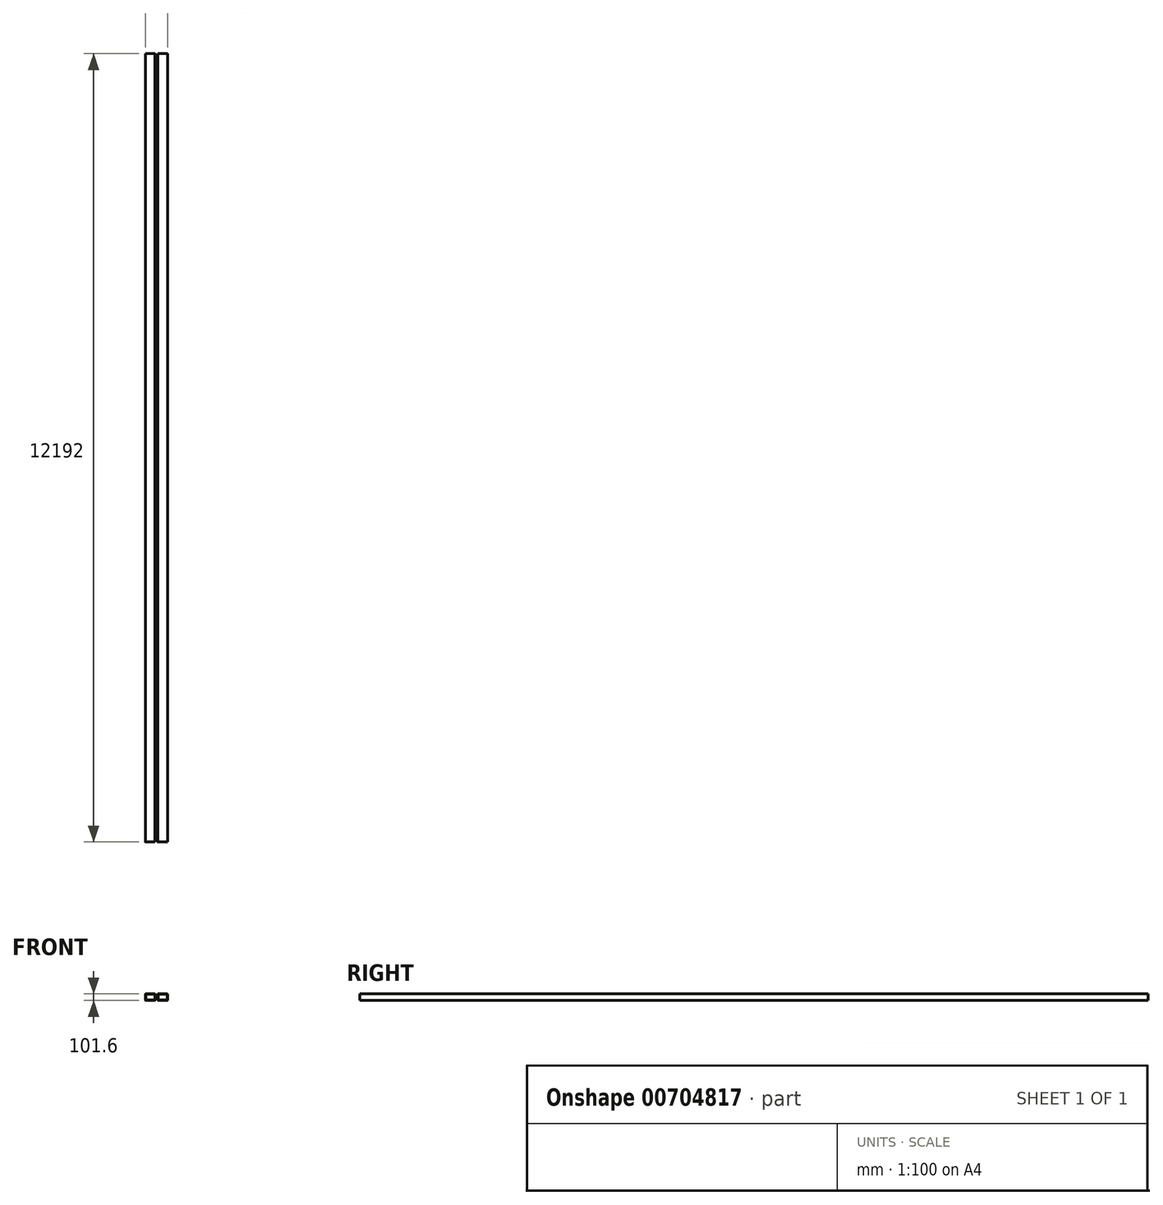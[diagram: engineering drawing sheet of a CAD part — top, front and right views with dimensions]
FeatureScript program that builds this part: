
annotation { "Feature Type Name" : "Feature", "Feature Type Description" : "" }
export const myFeature = defineFeature(function(context is Context, id is Id, definition is map)
    precondition{}
    {
        {
            var Q0;
            Q0=qCreatedBy(makeId("Front.planeOp"),FACE);
            var sketch = newSketch(context, id + "F0", { "sketchPlane" : qUnion([Q0])});
            skLineSegment(sketch, "E0.bottom", {"start": v(-6.35, 0) * mm, "end": v(-146.05, 0) * mm});
            skLineSegment(sketch, "E0.top", {"start": v(-6.35, 101.6) * mm, "end": v(-146.05, 101.6) * mm});
            skLineSegment(sketch, "E0.left", {"start": v(0, 6.35) * mm, "end": v(0, 95.25) * mm});
            skLineSegment(sketch, "E0.right", {"start": v(-152.4, 6.35) * mm, "end": v(-152.4, 95.25) * mm});
            skLineSegment(sketch, "E1.bottom", {"start": v(46.37, 0) * mm, "end": v(186.07, 0) * mm});
            skLineSegment(sketch, "E1.top", {"start": v(46.37, 101.6) * mm, "end": v(186.07, 101.6) * mm});
            skLineSegment(sketch, "E1.left", {"start": v(40.02, 6.35) * mm, "end": v(40.02, 95.25) * mm});
            skLineSegment(sketch, "E1.right", {"start": v(192.42, 6.35) * mm, "end": v(192.42, 95.25) * mm});
            skLineSegment(sketch, "E2.0", {"start": v(46.37, 6.35) * mm, "end": v(46.37, 95.25) * mm});
            skLineSegment(sketch, "E2.1", {"start": v(46.37, 6.35) * mm, "end": v(186.07, 6.35) * mm});
            skLineSegment(sketch, "E2.2", {"start": v(186.07, 6.35) * mm, "end": v(186.07, 95.25) * mm});
            skLineSegment(sketch, "E2.3", {"start": v(46.37, 95.25) * mm, "end": v(186.07, 95.25) * mm});
            skLineSegment(sketch, "E3", {"start": v(-146.05, 95.25) * mm, "end": v(-6.35, 95.25) * mm});
            skLineSegment(sketch, "E4", {"start": v(-6.35, 95.25) * mm, "end": v(-6.35, 6.35) * mm});
            skLineSegment(sketch, "E5", {"start": v(-6.35, 6.35) * mm, "end": v(-146.05, 6.35) * mm});
            skLineSegment(sketch, "E6", {"start": v(-146.05, 95.25) * mm, "end": v(-146.05, 6.35) * mm});
            skPoint(sketch, "E7.visualSharp", {"position": v(-152.4, 101.6) * mm});
            skArc(sketch, "E7.filletArc", {"start": v(-146.05, 101.6) * mm, "mid": v(-150.54, 99.74) * mm, "end": v(-152.4, 95.25) * mm});
            skPoint(sketch, "E8.visualSharp", {"position": v(-152.4, 0) * mm});
            skArc(sketch, "E8.filletArc", {"start": v(-152.4, 6.35) * mm, "mid": v(-150.54, 1.86) * mm, "end": v(-146.05, 0) * mm});
            skPoint(sketch, "E9.visualSharp", {"position": v(0, 0) * mm});
            skArc(sketch, "E9.filletArc", {"start": v(-6.35, 0) * mm, "mid": v(-1.86, 1.86) * mm, "end": v(0, 6.35) * mm});
            skPoint(sketch, "E10.visualSharp", {"position": v(0, 101.6) * mm});
            skArc(sketch, "E10.filletArc", {"start": v(0, 95.25) * mm, "mid": v(-1.86, 99.74) * mm, "end": v(-6.35, 101.6) * mm});
            skPoint(sketch, "E11.visualSharp", {"position": v(40.02, 101.6) * mm});
            skArc(sketch, "E11.filletArc", {"start": v(46.37, 101.6) * mm, "mid": v(41.88, 99.74) * mm, "end": v(40.02, 95.25) * mm});
            skPoint(sketch, "E12.visualSharp", {"position": v(192.42, 101.6) * mm});
            skArc(sketch, "E12.filletArc", {"start": v(192.42, 95.25) * mm, "mid": v(190.56, 99.74) * mm, "end": v(186.07, 101.6) * mm});
            skPoint(sketch, "E13.visualSharp", {"position": v(192.42, 0) * mm});
            skArc(sketch, "E13.filletArc", {"start": v(186.07, 0) * mm, "mid": v(190.56, 1.86) * mm, "end": v(192.42, 6.35) * mm});
            skPoint(sketch, "E14.visualSharp", {"position": v(40.02, 0) * mm});
            skArc(sketch, "E14.filletArc", {"start": v(40.02, 6.35) * mm, "mid": v(41.88, 1.86) * mm, "end": v(46.37, 0) * mm});
            skSolve(sketch);
        }
        {
            var Q0;
            Q0=makeQuery(id+"F0.imprint","IMPRINT",FACE,{"disambiguationData":[TD([[makeQuery(id+"F0.imprint","IMPRINT",EDGE,{"derivedFrom":sQuery(id+"F0.wireOp",EDGE,"E0.bottom")}),-1.0]])]});
            var Q1;
            Q1=makeQuery(id+"F0.imprint","IMPRINT",FACE,{"disambiguationData":[TD([[makeQuery(id+"F0.imprint","IMPRINT",EDGE,{"derivedFrom":sQuery(id+"F0.wireOp",EDGE,"E1.bottom")}),1.0]])]});
            extrude(context, id + "F1", {"entities" : qUnion([Q0, Q1]), "depth" : 12192 * mm});
        }
    });
